# Revit family: floodlight_fl_21_micro___pl43_5xa7764a4a1a_6fef
name_source: partatom
category: Lighting Fixtures
units: mm (PartAtom-declared; Revit-internal decimal feet)

## family parameters
Cut with Voids When Loaded = No
Host = Face
Light Source = No
Part Type = Normal
Room Calculation Point = No
Round Connector Dimension = Use Diameter
Shared = No

## types (1)
- --- (1 x LED, 3180 lm, 23.9 W, 4000K)
    Apparent Load = 24 VA
    CIE Flux Codes = 29 80 99 100 100
    Color Rendering = 70
    Color Temperature = 4000K
    Default Elevation = 1800 mm
    Description = Floodlight FL 21 micro, floodlight, primary light control with lens, of PMMA, primary optical cover: protective disc, of toughened safety glass, transparent, light distribution: PL43, light emission: direct distribution, installation type: surface-mounted, LED, High Power LED, rated luminous flux: 3.180lm, luminous efficacy: 133lm/W, light colour: 740, colour temperature: 4000K, control gear: ECG DALI, control: overheat protection, power reduction, constant luminous flux control, flexible luminous flux parameterisation, with terminal, 6-pole, mains connection: 220..240V, AC/DC, 0/50..60Hz, start of lifetime: 24W, end of lifetime: 25W, luminaire housing, of diecast aluminium, powder-coated, Siteco® metallic grey (DB 702S), corrosivity category C5 according to DIN EN ISO 12944, mounting bracket, of steel, galvanised, powder-coated, Siteco® metallic grey (DB 702S), protection rating (complete): IP66, insulation class (complete): insulation class II (safety insulation), certification: CE, impact resistance: IK07, permissible operating ambient temperature: -40..+40°C, permissible operating ambient temperature for outdoor applications: -40..+50°C, standard: DIN EN 12944, packaging unit: 1 piece

Light Distribution: PL43
    Height = 65 mm
    Lamp = 1 x LED
    Lamp Light Flux = 3180 lm
    Lamp Power = 23.9 W
    Lamp count = 1
    Length = 312 mm
    Luminous efficacy = 133 lm/W
    Manufacturer = Siteco
    ModVariant = No
    Model = 5XA7764A4A1A
    Number of Poles = 1
    OnlyDefault = Yes
    Power Factor = 1
    Product Name = Floodlight FL 21 micro | PL43
    Product group = floodlight | pylon top
    ProductGroupID = 6101
    Protection Class = Protection class II
    Protection Degree = IP 66
    RLX_Detail_Level = 1
    RlxData = <blob elided: 80041 chars, md5=bf336033>
    Socket = socket
    Standby Power = 0 W
    System Light Flux = 3180 lm
    System Power = 24 W
    Type Comments = factory setting: luminous flux: 100 % | dim-lin: 254 | 455 mA
    Type Image = l_1006880.jpg
    URL = http://relux.com
    VarID = @adj_089681
    Voltage = 0 V
    Weight = 0.00 kg
    Width = 230 mm

## geometry (parser evidence)
native form markers: Sweep x12
no freeform markers — native parametric forms only
